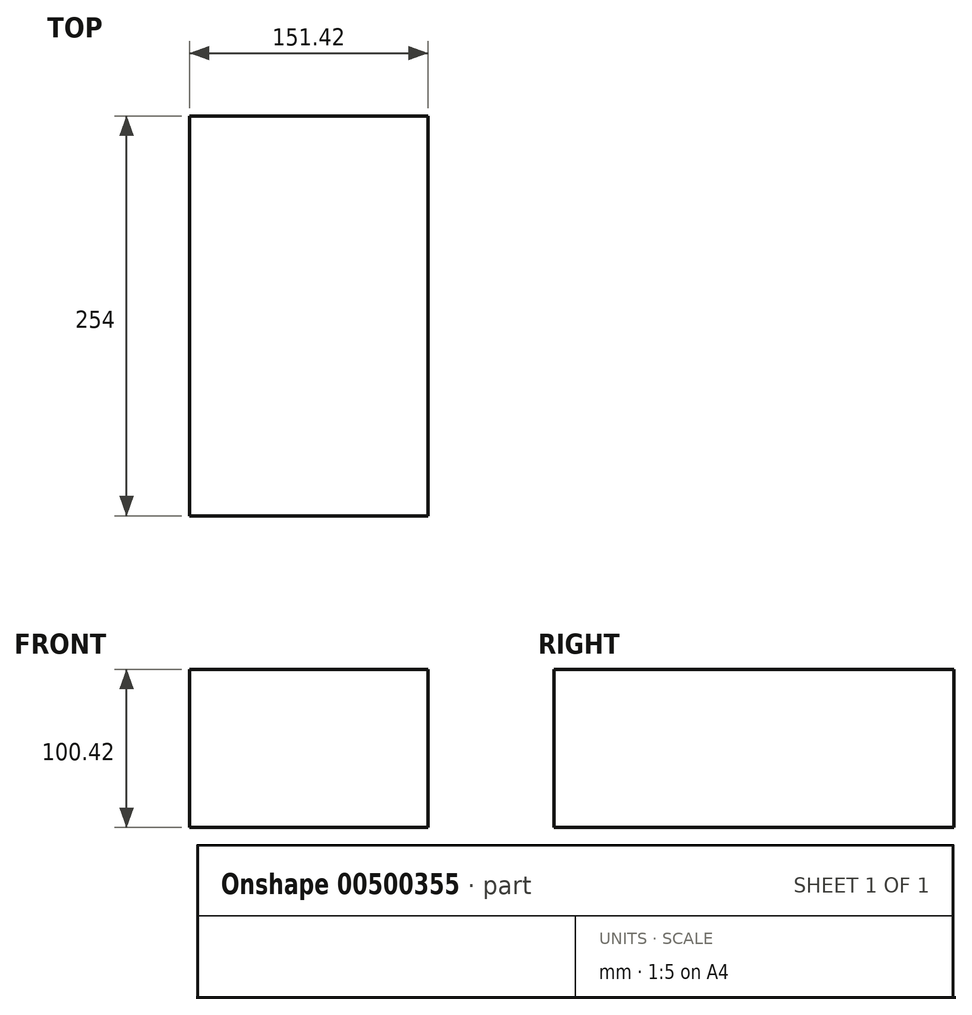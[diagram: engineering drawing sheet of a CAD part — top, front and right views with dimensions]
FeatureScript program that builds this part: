
annotation { "Feature Type Name" : "Feature", "Feature Type Description" : "" }
export const myFeature = defineFeature(function(context is Context, id is Id, definition is map)
    precondition{}
    {
        {
            var Q0;
            Q0=qCreatedBy(makeId("Front.planeOp"),FACE);
            var sketch = newSketch(context, id + "F0", { "sketchPlane" : qUnion([Q0])});
            skLineSegment(sketch, "E0.bottom", {"start": v(75.71, 50.2) * mm, "end": v(-75.71, 50.2) * mm});
            skLineSegment(sketch, "E0.top", {"start": v(75.71, -50.2) * mm, "end": v(-75.71, -50.2) * mm});
            skLineSegment(sketch, "E0.left", {"start": v(75.71, 50.2) * mm, "end": v(75.71, -50.2) * mm});
            skLineSegment(sketch, "E0.right", {"start": v(-75.71, 50.2) * mm, "end": v(-75.71, -50.2) * mm});
            skPoint(sketch, "E0.middle", {"position": v(0, 0) * mm});
            skSolve(sketch);
        }
        {
            var Q0;
            Q0 = qSketchRegion(id + "F0", true);
            extrude(context, id + "F1", {"entities" : qUnion([Q0]), "endBound" : BoundingType.SYMMETRIC, "depth" : 254 * mm});
        }
    });
